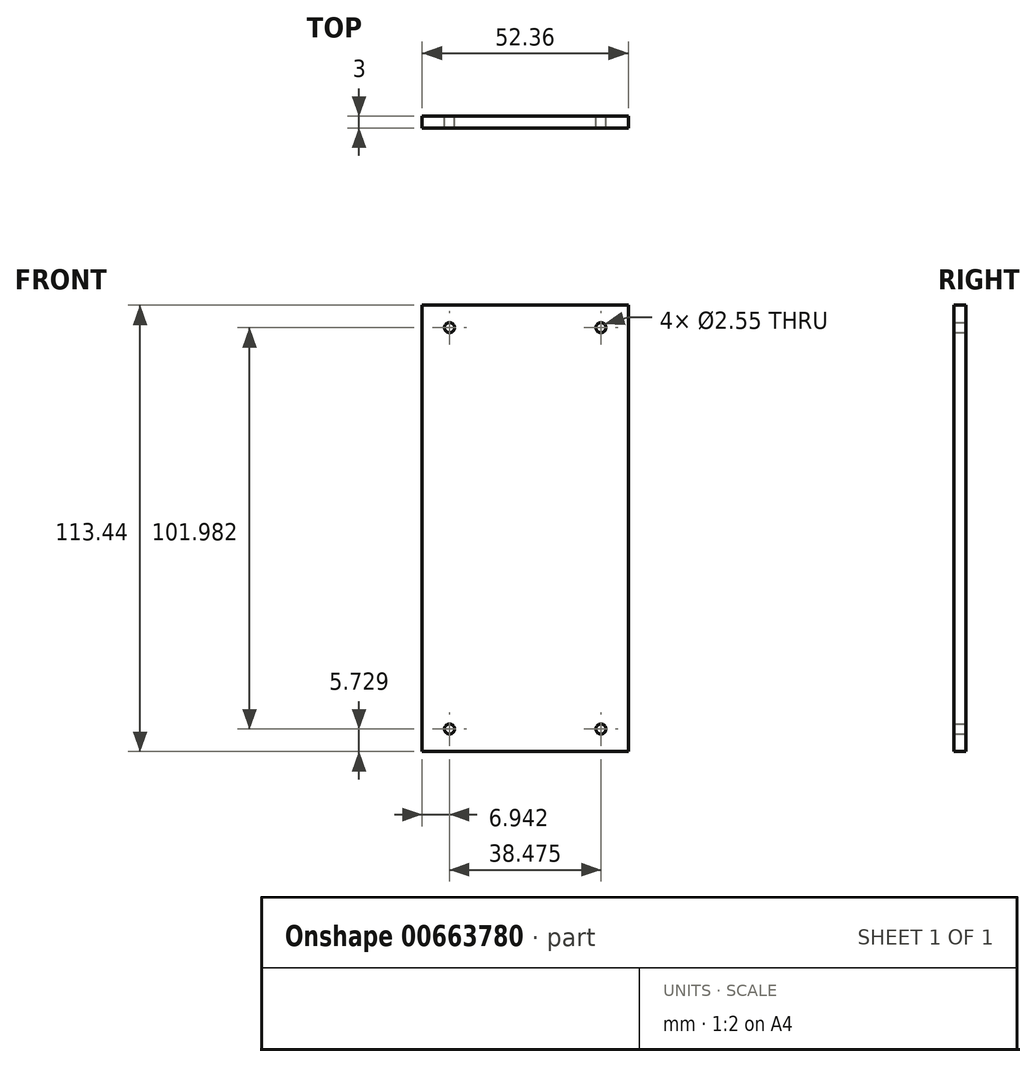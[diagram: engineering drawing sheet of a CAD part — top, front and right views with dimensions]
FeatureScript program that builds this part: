
annotation { "Feature Type Name" : "Feature", "Feature Type Description" : "" }
export const myFeature = defineFeature(function(context is Context, id is Id, definition is map)
    precondition{}
    {
        {
            var Q0;
            Q0=qCreatedBy(makeId("Front.planeOp"),FACE);
            var sketch = newSketch(context, id + "F0", { "sketchPlane" : qUnion([Q0])});
            skLineSegment(sketch, "E0.bottom", {"start": v(-26.18, 56.72) * mm, "end": v(26.18, 56.72) * mm});
            skLineSegment(sketch, "E0.top", {"start": v(-26.18, -56.72) * mm, "end": v(26.18, -56.72) * mm});
            skLineSegment(sketch, "E0.left", {"start": v(-26.18, 56.72) * mm, "end": v(-26.18, -56.72) * mm});
            skLineSegment(sketch, "E0.right", {"start": v(26.18, 56.72) * mm, "end": v(26.18, -56.72) * mm});
            skPoint(sketch, "E0.middle", {"position": v(0, 0) * mm});
            skCircle(sketch, "E1", {"center": v(-19.24, 51) * mm, "radius": 1.27 * mm});
            skLineSegment(sketch, "E2", {"start": v(0, 0) * mm, "end": v(0, 56.72) * mm, "construction": true});
            skLineSegment(sketch, "E3", {"start": v(0, 0) * mm, "end": v(-26.18, 0) * mm, "construction": true});
            skCircle(sketch, "E4.MirrorC", {"center": v(19.24, 51) * mm, "radius": 1.27 * mm});
            skCircle(sketch, "E5.MirrorC", {"center": v(-19.24, -51) * mm, "radius": 1.27 * mm});
            skCircle(sketch, "E6.MirrorC", {"center": v(19.24, -51) * mm, "radius": 1.27 * mm});
            skSolve(sketch);
        }
        {
            var Q0;
            Q0 = qSketchRegion(id + "F0", true);
            extrude(context, id + "F1", {"entities" : qUnion([Q0]), "depth" : 3 * mm, "offsetDistance" : 25 * mm});
        }
    });
